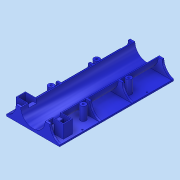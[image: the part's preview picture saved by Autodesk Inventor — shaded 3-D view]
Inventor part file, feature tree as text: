
AUTODESK INVENTOR PART (.ipt)
format: ipt  version: 2022 (Build 260153000, 153)  size: 292,864 bytes
history: native  units: in
note: dims shown in document units (in); Inventor stores cm internally (conversion verified against a paired STEP export)
features: other x3, projected_geometry x3, extrude x1, sketch x1
ambient origin geometry x8: Origin, YZ Plane, XZ Plane, XY Plane, X Axis, Y Axis, Z Axis, Center Point
bodies: Solid1 (feature_tree)
feature tree (8):
  other  "electronics.ipt"
  extrude  "Extrusion1"  Depth=0.9252in TaperAngle=0.0deg
  other  "Solid5::electronics.ipt"
  other  "TaggingFeature1"
  sketch  "Sketch1"  dims[d0=0.3937in d1=0.9252in d2=0.0in]
  projected_geometry  "Projected Loop1"
  projected_geometry  "Projected Loop2"
  projected_geometry  "Projected Loop3"
